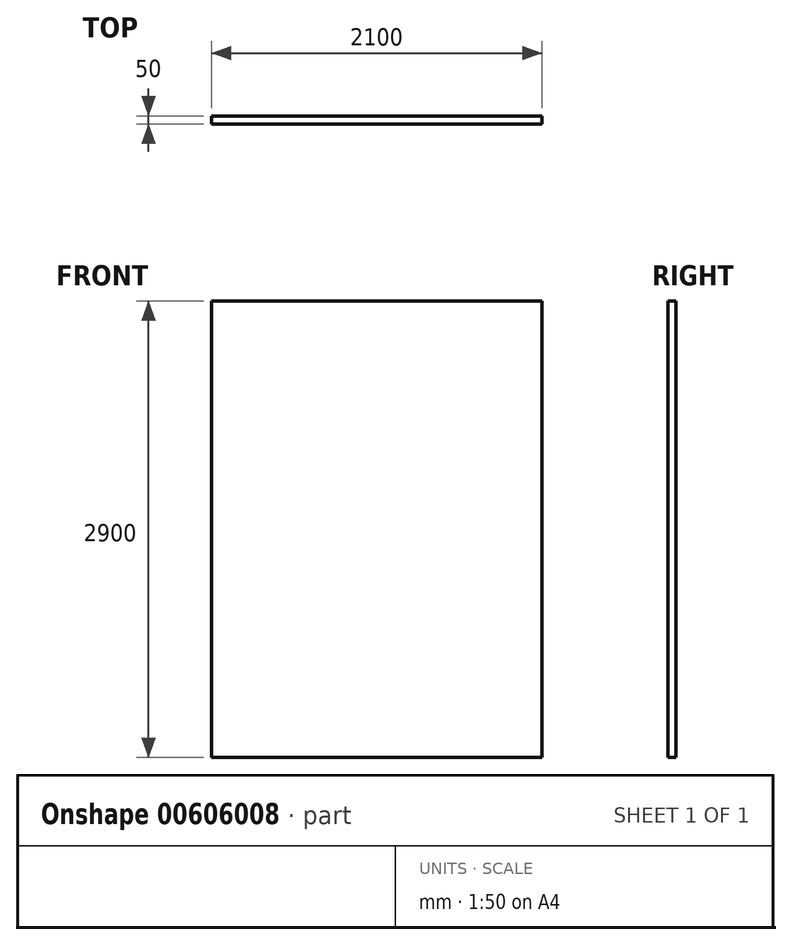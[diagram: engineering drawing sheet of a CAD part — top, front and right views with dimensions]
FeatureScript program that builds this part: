
annotation { "Feature Type Name" : "Feature", "Feature Type Description" : "" }
export const myFeature = defineFeature(function(context is Context, id is Id, definition is map)
    precondition{}
    {
        {
            var Q0;
            Q0=qCreatedBy(makeId("Top.planeOp"),FACE);
            var sketch = newSketch(context, id + "F0", { "sketchPlane" : qUnion([Q0]), "disableImprinting" : false});
            skLineSegment(sketch, "E0.bottom", {"start": v(1050, -25) * mm, "end": v(-1050, -25) * mm});
            skLineSegment(sketch, "E0.top", {"start": v(1050, 25) * mm, "end": v(-1050, 25) * mm});
            skLineSegment(sketch, "E0.left", {"start": v(1050, -25) * mm, "end": v(1050, 25) * mm});
            skLineSegment(sketch, "E0.right", {"start": v(-1050, -25) * mm, "end": v(-1050, 25) * mm});
            skPoint(sketch, "E0.middle", {"position": v(0, 0) * mm});
            skSolve(sketch);
        }
        {
            var Q0;
            Q0=makeQuery(id+"F0.imprint","IMPRINT",FACE,{"disambiguationData":[TD([[makeQuery(id+"F0.imprint","IMPRINT",EDGE,{"derivedFrom":sQuery(id+"F0.wireOp",EDGE,"E0.bottom")}),-1.0]])]});
            extrude(context, id + "F1", {"entities" : qUnion([Q0]), "flatOperationType" : FlatOperationType.REMOVE, "depth" : 2900 * mm, "offsetDistance" : 25 * mm, "startOffsetBound" : StartOffsetType.BLIND, "startOffsetDistance" : 25 * mm, "domain" : OperationDomain.MODEL});
        }
    });
